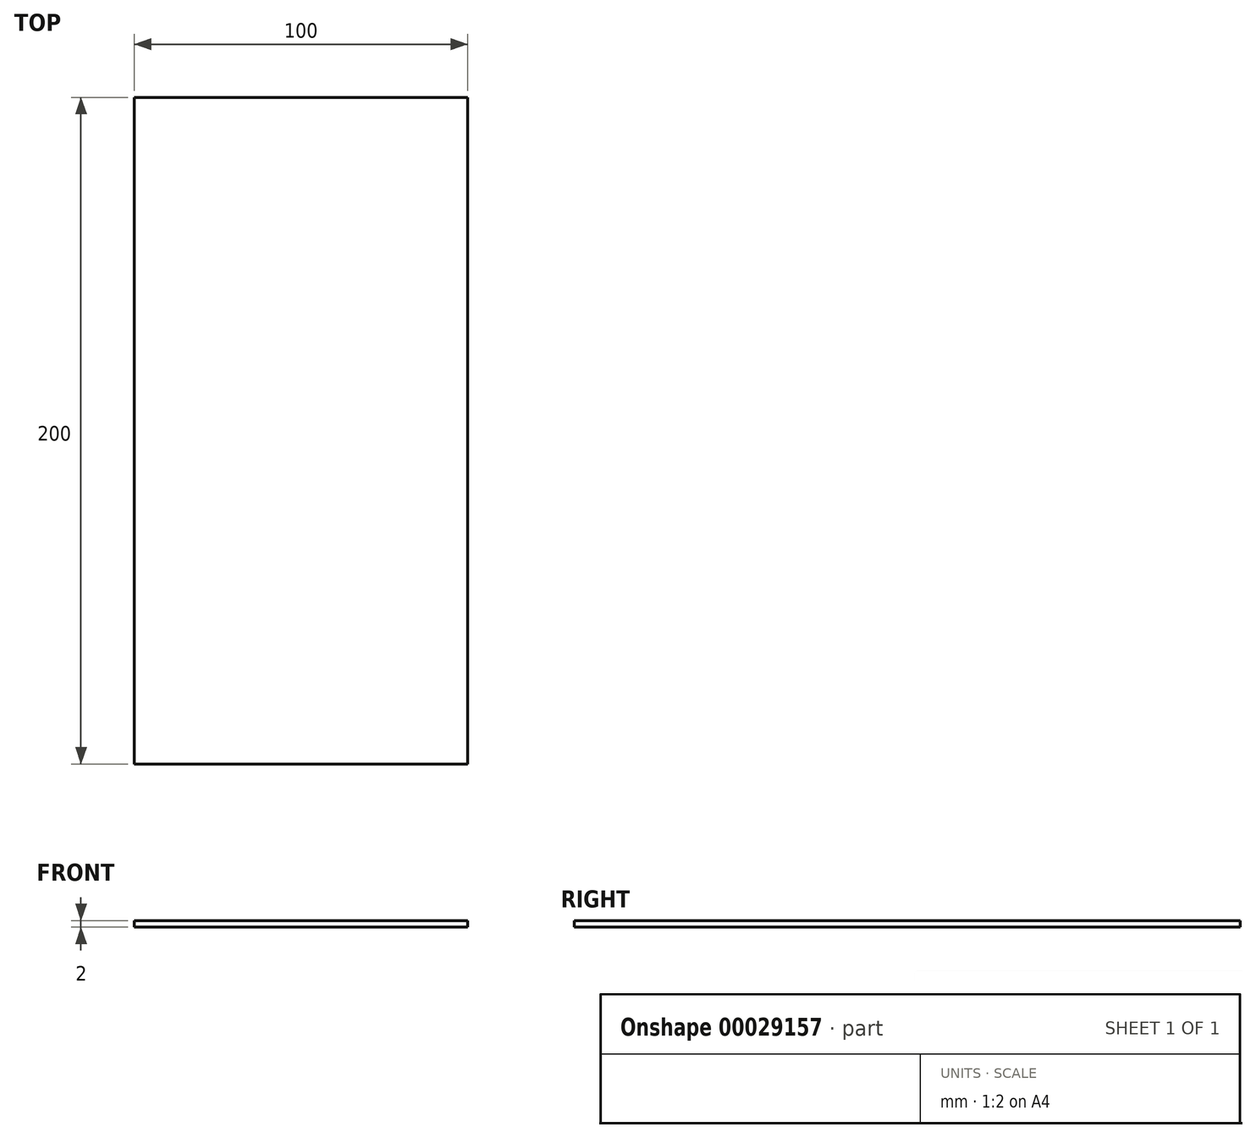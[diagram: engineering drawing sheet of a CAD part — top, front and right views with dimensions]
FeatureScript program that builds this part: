
annotation { "Feature Type Name" : "Feature", "Feature Type Description" : "" }
export const myFeature = defineFeature(function(context is Context, id is Id, definition is map)
    precondition{}
    {
        {
            var Q0;
            Q0=qCreatedBy(makeId("Top.planeOp"),FACE);
            var sketch = newSketch(context, id + "F0", { "sketchPlane" : qUnion([Q0])});
            skLineSegment(sketch, "E0.bottom", {"start": v(0, 0) * mm, "end": v(100, 0) * mm});
            skLineSegment(sketch, "E0.top", {"start": v(0, 200) * mm, "end": v(100, 200) * mm});
            skLineSegment(sketch, "E0.left", {"start": v(0, 0) * mm, "end": v(0, 200) * mm});
            skLineSegment(sketch, "E0.right", {"start": v(100, 0) * mm, "end": v(100, 200) * mm});
            skSolve(sketch);
        }
        {
            var Q0;
            Q0 = qSketchRegion(id + "F0", true);
            extrude(context, id + "F1", {"entities" : qUnion([Q0]), "depth" : 2 * mm});
        }
    });
